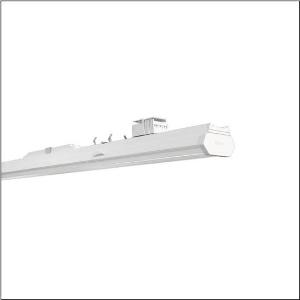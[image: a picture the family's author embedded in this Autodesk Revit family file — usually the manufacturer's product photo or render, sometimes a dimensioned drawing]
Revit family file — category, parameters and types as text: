
# Revit family: licross_r__11_protected_mo_51td12dn495g3c_9d50
name_source: partatom
category: Lighting Fixtures
units: mm (PartAtom-declared; Revit-internal decimal feet)

## family parameters
Cut with Voids When Loaded = No
Host = Face
Light Source = No
Part Type = Normal
Room Calculation Point = No
Round Connector Dimension = Use Diameter
Shared = No

## types (1)
- --- (1 x LED, 980 lm, 6.8 W, 4000K)
    Apparent Load = 7 VA
    CIE Flux Codes = 73 92 98 99 100
    Color Rendering = 80
    Color Temperature = 4000K
    Default Elevation = 1800 mm
    Description = Licross® 11 Protected MO, luminaire insert, of sheet steel, galvanised, coil coated, white, length: 1.500mm, width: 90mm, height: 101mm, LED rated luminous flux: 9.980lm, light colour: 840, control gear: DALI 2, with plug, 6-pole, with phase selection, for trunking rail, 14-core, mains connection: 220..240V, AC, 50/60Hz, rated input power: 61W, for trunking rail, 14-core, halogen-free wiring, for emergency light function, converter,control gear: single battery element, battery: LiFeP04, 9Ah, primary light control with lens, of plastic, primary optical cover: cover, of PMMA, light emission: direct distribution, primary light characteristic: symmetric, protection rating (complete): IP54, insulation class (complete): insulation class I (protective earthing), certification: CE, UKCA, protection symbol: D if used in an environment with non-conductive dust loads with corresponding accessories, impact resistance: IK06, permissible ambient temperature for indoor applications: +5..+35°C, standard: EN 60598-2-22, LABS conformity tested according to VDMA 24364:2018-05, reducing of maximum allowable ambient temperature of 5°C with ceiling mounting, corresponds to IFS (International Featured Standards) requirements for safety and quality in the food industry, packaging unit: 1 piece
    Height = 92 mm
    Lamp = 1 x LED
    Lamp Light Flux = 980 lm
    Lamp Power = 6.8 W
    Lamp count = 1
    Length = 1500 mm
    Luminous efficacy = 144 lm/W
    Manufacturer = Siteco
    ModVariant = No
    Model = 51TD12DN495G3C
    Mounting Place = Ceiling
    Mounting Type = Pendant
    Number of Poles = 1
    OnlyDefault = Yes
    Power Factor = 1
    Product Name = Licross® 11 Protected MO
    Product group = luminaire insert
    ProductGroupID = 901
    Protection Class = Protection class I
    Protection Degree = IP 54
    RLX_Detail_Level = 1
    RLX_Emergency_Light_Flux = 0 lm
    RLX_Emergency_Type = 0
    RLX_Emergency_Type_DB = No
    RlxData = <blob elided: 24765 chars, md5=37d3897c>
    Socket = socket
    Standby Power = 0 W
    System Light Flux = 980 lm
    System Power = 7 W
    Type Comments = : emergency light operation: 3 h
    Type Image = l_1256145.jpg
    URL = http://relux.com
    VarID = @adj_041217
    Voltage = 0 V
    Weight = 0.00 kg
    Width = 88 mm

## geometry (parser evidence)
native form markers: Blend x4, Sweep x12
no freeform markers — native parametric forms only
